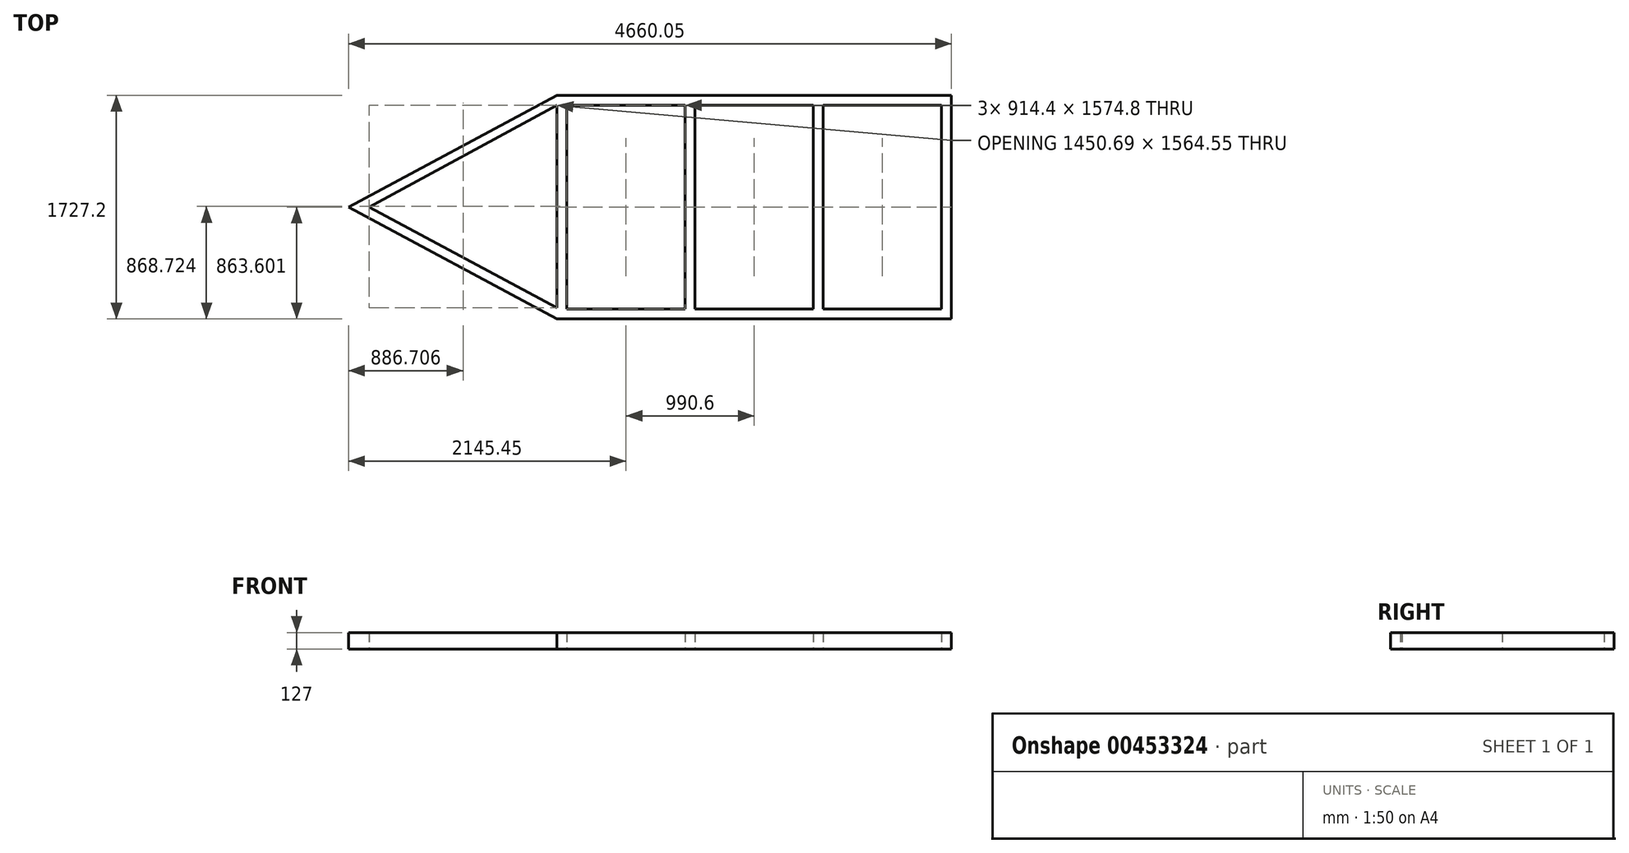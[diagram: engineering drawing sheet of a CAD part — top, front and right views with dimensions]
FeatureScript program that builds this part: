
annotation { "Feature Type Name" : "Feature", "Feature Type Description" : "" }
export const myFeature = defineFeature(function(context is Context, id is Id, definition is map)
    precondition{}
    {
        {
            var Q0;
            Q0=qCreatedBy(makeId("Top.planeOp"),FACE);
            var sketch = newSketch(context, id + "F0", { "sketchPlane" : qUnion([Q0])});
            skLineSegment(sketch, "E0.bottom", {"start": v(-476.31, 291.03) * mm, "end": v(2571.69, 291.03) * mm});
            skLineSegment(sketch, "E0.top", {"start": v(-476.31, -1436.17) * mm, "end": v(2571.69, -1436.17) * mm});
            skLineSegment(sketch, "E0.left", {"start": v(-476.31, 291.03) * mm, "end": v(-476.31, -1436.17) * mm});
            skLineSegment(sketch, "E0.right", {"start": v(2571.69, 291.03) * mm, "end": v(2571.69, -1436.17) * mm});
            skLineSegment(sketch, "E1.bottom", {"start": v(-400.11, 214.83) * mm, "end": v(2495.49, 214.83) * mm});
            skLineSegment(sketch, "E1.top", {"start": v(-400.11, -1359.97) * mm, "end": v(2495.49, -1359.97) * mm});
            skLineSegment(sketch, "E1.left", {"start": v(-400.11, 214.83) * mm, "end": v(-400.11, -1359.97) * mm});
            skLineSegment(sketch, "E1.right", {"start": v(2495.49, 214.83) * mm, "end": v(2495.49, -1359.97) * mm});
            skLineSegment(sketch, "E2", {"start": v(-476.31, 291.03) * mm, "end": v(-2088.36, -572.57) * mm});
            skLineSegment(sketch, "E3", {"start": v(-476.31, -1436.17) * mm, "end": v(-2088.36, -572.57) * mm});
            skLineSegment(sketch, "E4", {"start": v(-476.31, 214.83) * mm, "end": v(-1927, -572.57) * mm});
            skLineSegment(sketch, "E5", {"start": v(-1927, -572.57) * mm, "end": v(-476.31, -1349.72) * mm});
            skLineSegment(sketch, "E6", {"start": v(514.29, 214.83) * mm, "end": v(514.29, -1359.97) * mm});
            skLineSegment(sketch, "E7", {"start": v(590.49, 214.83) * mm, "end": v(590.49, -1359.97) * mm});
            skLineSegment(sketch, "E8", {"start": v(1504.89, 214.83) * mm, "end": v(1504.89, -1359.97) * mm});
            skLineSegment(sketch, "E9", {"start": v(1581.09, 214.83) * mm, "end": v(1581.09, -1359.97) * mm});
            skSolve(sketch);
        }
        {
            var Q0;
            {var subQ0=sQuery(id+"F0.wireOp",EDGE,"E2");Q0=makeQuery(id+"F0.imprint","IMPRINT",FACE,{"disambiguationData":[TD([[makeQuery(id+"F0.imprint","IMPRINT",EDGE,{"derivedFrom":subQ0}),1.0]])]});}
            var Q1;
            {var subQ13=sQuery(id+"F0.wireOp",EDGE,"E0.bottom");Q1=makeQuery(id+"F0.imprint","IMPRINT",FACE,{"disambiguationData":[TD([[makeQuery(id+"F0.imprint","IMPRINT",EDGE,{"derivedFrom":subQ13}),-1.0]])]});}
            var Q2;
            {var subQ0=sQuery(id+"F0.wireOp",EDGE,"E6");Q2=makeQuery(id+"F0.imprint","IMPRINT",FACE,{"disambiguationData":[TD([[makeQuery(id+"F0.imprint","IMPRINT",EDGE,{"derivedFrom":subQ0}),1.0]])]});}
            var Q3;
            {var subQ0=sQuery(id+"F0.wireOp",EDGE,"E8");Q3=makeQuery(id+"F0.imprint","IMPRINT",FACE,{"disambiguationData":[TD([[makeQuery(id+"F0.imprint","IMPRINT",EDGE,{"derivedFrom":subQ0}),1.0]])]});}
            extrude(context, id + "F1", {"entities" : qUnion([Q0, Q1, Q2, Q3]), "depth" : 127 * mm});
        }
    });
